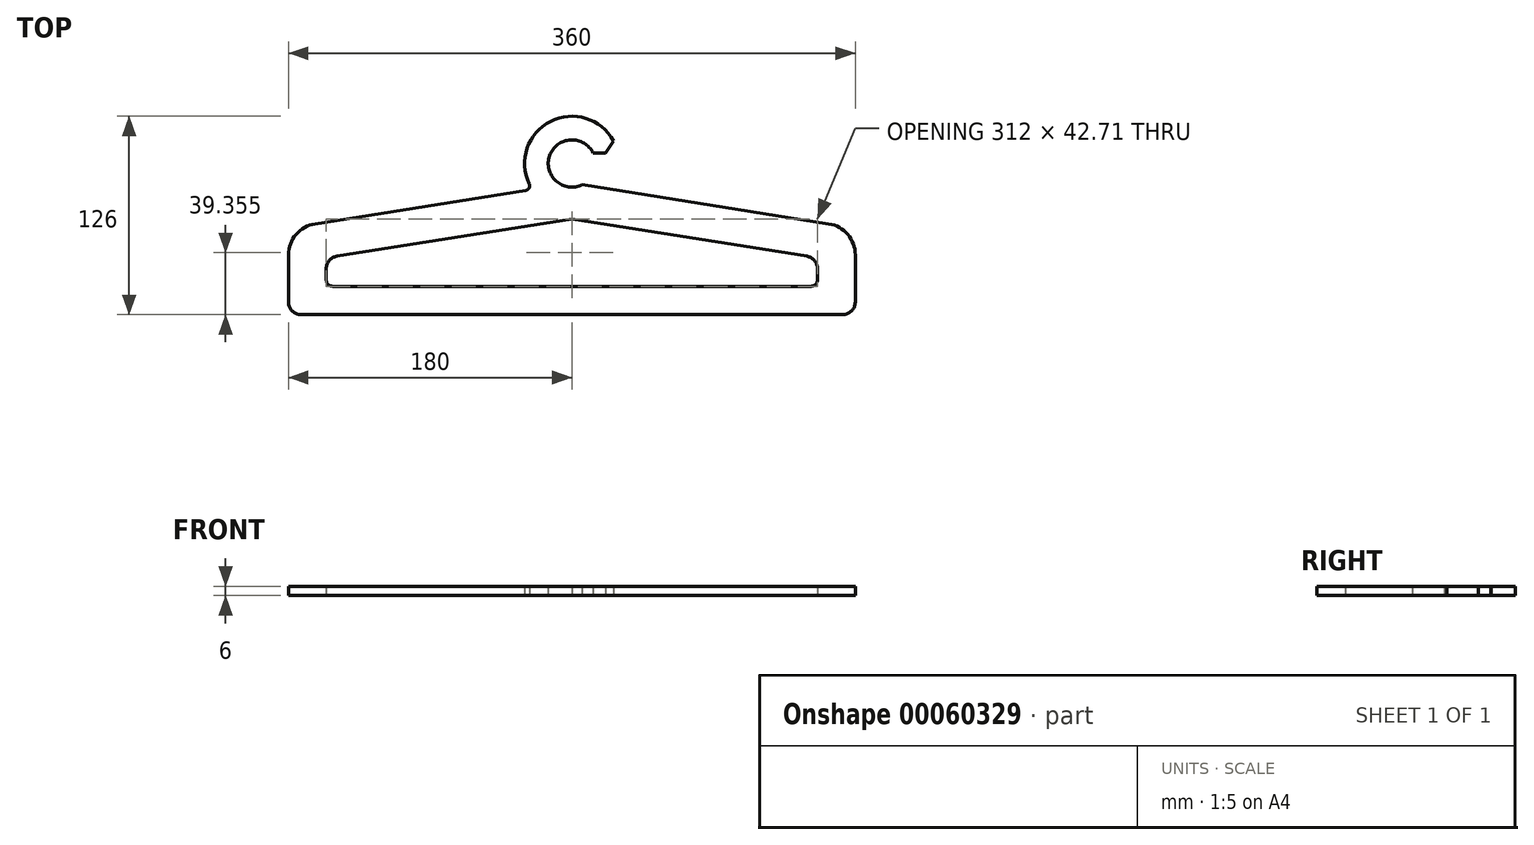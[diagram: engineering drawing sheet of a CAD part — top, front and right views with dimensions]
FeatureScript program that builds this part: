
annotation { "Feature Type Name" : "Feature", "Feature Type Description" : "" }
export const myFeature = defineFeature(function(context is Context, id is Id, definition is map)
    precondition{}
    {
        {
            var Q0;
            Q0=qCreatedBy(makeId("Top.planeOp"),FACE);
            var sketch = newSketch(context, id + "F0", { "sketchPlane" : qUnion([Q0])});
            skLineSegment(sketch, "E0", {"start": v(0, 185.22) * mm, "end": v(0, -236.47) * mm, "construction": true});
            skArc(sketch, "E1", {"start": v(0, 134.06) * mm, "mid": v(-25.36, 120.08) * mm, "end": v(-27.1, 91.18) * mm});
            skLineSegment(sketch, "E2", {"start": v(-29.33, 86.92) * mm, "end": v(-163.13, 65.73) * mm});
            skLineSegment(sketch, "E3", {"start": v(-180, 45.98) * mm, "end": v(-180, 16.06) * mm});
            skLineSegment(sketch, "E4", {"start": v(-172, 8.06) * mm, "end": v(0, 8.06) * mm});
            skLineSegment(sketch, "E5", {"start": v(0, 68.77) * mm, "end": v(-149.25, 45.13) * mm});
            skLineSegment(sketch, "E6", {"start": v(-156, 37.23) * mm, "end": v(-156, 30.06) * mm});
            skLineSegment(sketch, "E7", {"start": v(-152, 26.06) * mm, "end": v(0, 26.06) * mm});
            skPoint(sketch, "E8.visualSharp", {"position": v(-180, 63.06) * mm});
            skArc(sketch, "E8.filletArc", {"start": v(-163.13, 65.73) * mm, "mid": v(-175.2, 58.97) * mm, "end": v(-180, 45.98) * mm});
            skPoint(sketch, "E9.visualSharp", {"position": v(-156, 44.06) * mm});
            skArc(sketch, "E9.filletArc", {"start": v(-149.25, 45.13) * mm, "mid": v(-154.08, 42.42) * mm, "end": v(-156, 37.23) * mm});
            skPoint(sketch, "E10.visualSharp", {"position": v(-156, 26.06) * mm});
            skArc(sketch, "E10.filletArc", {"start": v(-156, 30.06) * mm, "mid": v(-154.83, 27.23) * mm, "end": v(-152, 26.06) * mm});
            skPoint(sketch, "E11.visualSharp", {"position": v(-180, 8.06) * mm});
            skArc(sketch, "E11.filletArc", {"start": v(-180, 16.06) * mm, "mid": v(-177.66, 10.4) * mm, "end": v(-172, 8.06) * mm});
            skLineSegment(sketch, "E12.MirrorCS", {"start": v(156, 37.23) * mm, "end": v(156, 30.06) * mm});
            skArc(sketch, "E13.MirrorCS", {"start": v(149.25, 45.13) * mm, "mid": v(154.08, 42.42) * mm, "end": v(156, 37.23) * mm});
            skArc(sketch, "E14.MirrorCS", {"start": v(156, 30.06) * mm, "mid": v(154.83, 27.23) * mm, "end": v(152, 26.06) * mm});
            skArc(sketch, "E15.MirrorCS", {"start": v(180, 16.06) * mm, "mid": v(177.66, 10.4) * mm, "end": v(172, 8.06) * mm});
            skLineSegment(sketch, "E16.MirrorCS", {"start": v(25.08, 87.6) * mm, "end": v(163.13, 65.73) * mm});
            skLineSegment(sketch, "E17.MirrorCS", {"start": v(0, 68.77) * mm, "end": v(149.25, 45.13) * mm});
            skLineSegment(sketch, "E18.MirrorCS", {"start": v(172, 8.06) * mm, "end": v(0, 8.06) * mm});
            skPoint(sketch, "E19.MirrorP", {"position": v(156, 26.06) * mm});
            skLineSegment(sketch, "E20.MirrorCS", {"start": v(180, 45.98) * mm, "end": v(180, 16.06) * mm});
            skLineSegment(sketch, "E21.MirrorCS", {"start": v(152, 26.06) * mm, "end": v(0, 26.06) * mm});
            skArc(sketch, "E22.MirrorCS", {"start": v(163.13, 65.73) * mm, "mid": v(175.2, 58.97) * mm, "end": v(180, 45.98) * mm});
            skPoint(sketch, "E23.MirrorP", {"position": v(156, 44.06) * mm});
            skPoint(sketch, "E24.MirrorP", {"position": v(180, 63.06) * mm});
            skPoint(sketch, "E25.MirrorP", {"position": v(180, 8.06) * mm});
            skArc(sketch, "E26.MirrorCS", {"start": v(0, 134.06) * mm, "mid": v(18.78, 127.45) * mm, "end": v(29.3, 110.54) * mm});
            skCircle(sketch, "E27", {"center": v(0, 104.06) * mm, "radius": 15 * mm});
            skLineSegment(sketch, "E28", {"start": v(25.08, 87.6) * mm, "end": v(6.5, 90.54) * mm});
            skPoint(sketch, "E29.newPointA", {"position": v(25.08, 87.6) * mm});
            skLineSegment(sketch, "E30", {"start": v(13.53, 110.54) * mm, "end": v(29.3, 110.54) * mm});
            skLineSegment(sketch, "E31", {"start": v(21.4, 110.54) * mm, "end": v(26.34, 118.41) * mm});
            skPoint(sketch, "E32.visualSharp", {"position": v(-25.08, 87.6) * mm});
            skArc(sketch, "E32.filletArc", {"start": v(-29.33, 86.92) * mm, "mid": v(-27.15, 88.49) * mm, "end": v(-27.1, 91.18) * mm});
            skSolve(sketch);
        }
        {
            var Q0;
            Q0=makeQuery(id+"F0.imprint","IMPRINT",FACE,{"disambiguationData":[TD([[makeQuery(id+"F0.imprint","IMPRINT",EDGE,{"derivedFrom":sQuery(id+"F0.wireOp",EDGE,"E1")}),1.0]])]});
            extrude(context, id + "F1", {"entities" : qUnion([Q0]), "depth" : 6 * mm});
        }
    });
